# Revit family: Comfort_Window_C_Top_Hung_Standard
name_source: partatom
category: Windows
revit_build: Autodesk Revit 2014 (Build: 20130308_1515(x64)
units: mm (PartAtom-declared; Revit-internal decimal feet)

## types (2) — shared parameters
DG Gasket Thickness = 12 mm  [stored 0.0393701 ft]
Description = Comfort Window, Top Hung, Type C
Double Glazing Gasket Finish = Double Glazing Gasket Material
Frame Depth = 33 mm  [stored 0.108268 ft]
Frame Edge Thickness = 26 mm
Limit Fixed Pane Height Max = 1800 mm  [stored 5.90551 ft]
Limit Fixed Pane Height Min = 200 mm  [stored 0.656168 ft]
Limit Fixed Pane Width Max = 1800 mm  [stored 5.90551 ft]
Limit Fixed Pane Width Min = 200 mm  [stored 0.656168 ft]
Limit Sash Height Max = 1200 mm
Limit Sash Height Min = 300 mm  [stored 0.984252 ft]
Limit Sash Width Max = 1200 mm
Limit Sash Width Min = 300 mm  [stored 0.984252 ft]
Limit Window Height Max = 1275 mm  [stored 4.18307 ft]
Limit Window Height Min = 375 mm  [stored 1.23031 ft]
Manufacturer = Crealco
Max System DG One Piece Thickness = 4 mm  [stored 0.0131234 ft]
Max System DG Unit Thickness = 20 mm  [stored 0.0656168 ft]
Model = Comfort Window
Mullion Width = 27 mm  [stored 0.0885827 ft]
Rough Height = 590 mm  [stored 1.9357 ft]
Rough Width = 902 mm  [stored 2.95932 ft]
Sash Frame Gap = 5 mm  [stored 0.0164042 ft]
Sash Frame Side Gap = 12 mm  [stored 0.0393701 ft]
Sash Side Gap = 38 mm
Set Sash Width = 515 mm  [stored 1.68963 ft]
URL = http://www.crealco.co.za
Window Height = 590 mm  [stored 1.9357 ft]
zero-valued in all types: Visual Light Transmittance

## per-type parameters (varying)
| type | Clearvue SHGC Value | Clearvue U Value | Energy Advantage SHGC Value | Energy Advantage U Value | Intruderprufe LowE SHGC Value | Intruderprufe LowE U Value | Intruderprufe SHGC Value | Intruderprufe U Value | SmartGlass Elite SHGC Value | SmartGlass Elite U Value | SmartGlass Plus SHGC Value | SmartGlass Plus U Value | SmartGlass Standard SHGC Value | SmartGlass Standard U Value | SmartGlass Superior SHGC Value | SmartGlass Superior U Value | Window Width |
| Comfort-1806TT | 0.542 | 6.12 | 0.487 | 4.86 | 0.462 | 4.74 | 0.517 | 6.02 | 0.269 | 3.64 | 0.363 | 3.77 | 0.485 | 4.24 | 0.235 | 3.65 | 1790 mm  [stored 5.8727 ft] |
| Comfort-2406TT | 0.567 | 6.1 | 0.509 | 4.76 | 0.483 | 4.64 | 0.54 | 6 | 0.279 | 3.49 | 0.379 | 3.62 | 0.507 | 4.12 | 0.244 | 3.49 | 2390 mm  [stored 7.84121 ft] |

note: [stored X ft] marks values corroborated as IEEE doubles in the binary element streams (Revit-internal decimal feet)

## geometry (parser evidence)
native form markers: Sweep x18
no freeform markers — native parametric forms only
